# Revit family: Приствольная решётка (квадратная) Р-07
name_source: partatom
category: Антураж
revit_build: Autodesk Revit 2017 (Build: 20160225_1515(x64)
units: mm (PartAtom-declared; Revit-internal decimal feet)

## family parameters
Всегда вертикально = Да
Источник визуального образа = Геометрия семейства
На основе рабочей плоскости = Нет
Общий = Нет
При загрузке вырезать с полостями = Нет
Точка расчета площади = Нет

## types (2) — shared parameters
ADSK_Код изделия = 10269
ADSK_Материал решетки = Чугун, серый
URL = https://hobbyka.ru
Изготовитель = ООО "Хоббика"
Стоимость = 11994 $

## per-type parameters (varying)
| type | 1000х1000 | 1200x1200 | ADSK_Размер_Высота | ADSK_Размер_Длина | ADSK_Размер_Ширина | Высота |
| Приствольная решётка (квадратная) Р-07 1000х1000 | Да | Нет | 25 мм | 1000 мм | 1000 мм | 0 мм |
| Приствольная решётка (квадратная) Р-07 1200х1200 | Нет | Да | 0 мм | 1200 мм | 1200 мм | 25 мм |

note: column(s) folded — value = type name in every type: ADSK_Наименование
